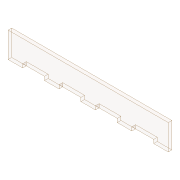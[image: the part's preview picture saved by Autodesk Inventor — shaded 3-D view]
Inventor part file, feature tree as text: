
AUTODESK INVENTOR PART (.ipt)
format: ipt  version: 2020 (Build 240168000, 168)  size: 112,640 bytes
history: native  units: mm
features: extrude x2, sketch x2
ambient origin geometry x8: Origin, YZ Plane, XZ Plane, XY Plane, X Axis, Y Axis, Z Axis, Center Point
bodies: Solid1 (feature_tree)
feature tree (4):
  extrude  "Base"  Depth=30.0mm
  extrude  "Encaixe"  Depth=20.0mm
  sketch  "Sketch1"  dims[d0=220.0mm d1=30.0mm]
  sketch  "Sketch2"  dims[d2=5.0mm d3=0.0mm d4=20.0mm d5=5.0mm d6=50.0mm d8=50.0mm d9=10.0mm d11=10.0mm d13=5.0mm d14=0.0mm]
